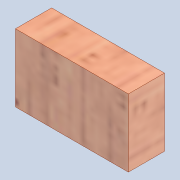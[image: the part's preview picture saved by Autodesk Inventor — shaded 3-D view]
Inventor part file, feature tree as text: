
AUTODESK INVENTOR PART (.ipt)
format: ipt  version: 2020 (Build 240168000, 168)  size: 122,368 bytes
history: native  units: mm
features: extrude x1, sketch x1
ambient origin geometry x8: Origin, YZ Plane, XZ Plane, XY Plane, X Axis, Y Axis, Z Axis, Center Point
bodies: Solid1 (feature_tree)
feature tree (2):
  extrude  "Extrusion1"  Depth=25.0mm
  sketch  "Sketch1"  dims[d0=15.0mm d1=25.0mm d2=8.0mm d3=0.0mm]
